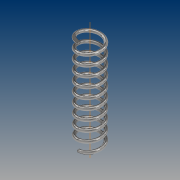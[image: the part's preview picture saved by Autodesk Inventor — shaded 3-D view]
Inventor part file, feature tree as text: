
AUTODESK INVENTOR PART (.ipt)
format: ipt  version: 2021 (Build 250183000, 183)  size: 313,856 bytes
history: native  units: mm
features: sketch x2, extrude x1, helix x1
ambient origin geometry x8: Origin, YZ Plane, XZ Plane, XY Plane, X Axis, Y Axis, Z Axis, Center Point
bodies: Solid1 (feature_tree)
feature tree (4):
  extrude  "Extrusion1"  Depth=3.6mm
  helix  "Coil1"  [1 undecoded]
  sketch  "Sketch1"  dims[d0=1.0mm d1=3.6mm d2=30.0mm d3=0.0mm]
  sketch  "Sketch2"  dims[d4=3.0mm d5=30.0mm d6=10.0mm d7=0.0mm d8=90.0deg d9=90.0deg d10=0.0mm d11=0.0mm]
note: 1 required parameter value undecoded (feature->parameter linkage not recoverable at this tier; creation-order binding heuristic only, values carry confidence <= 0.55)
